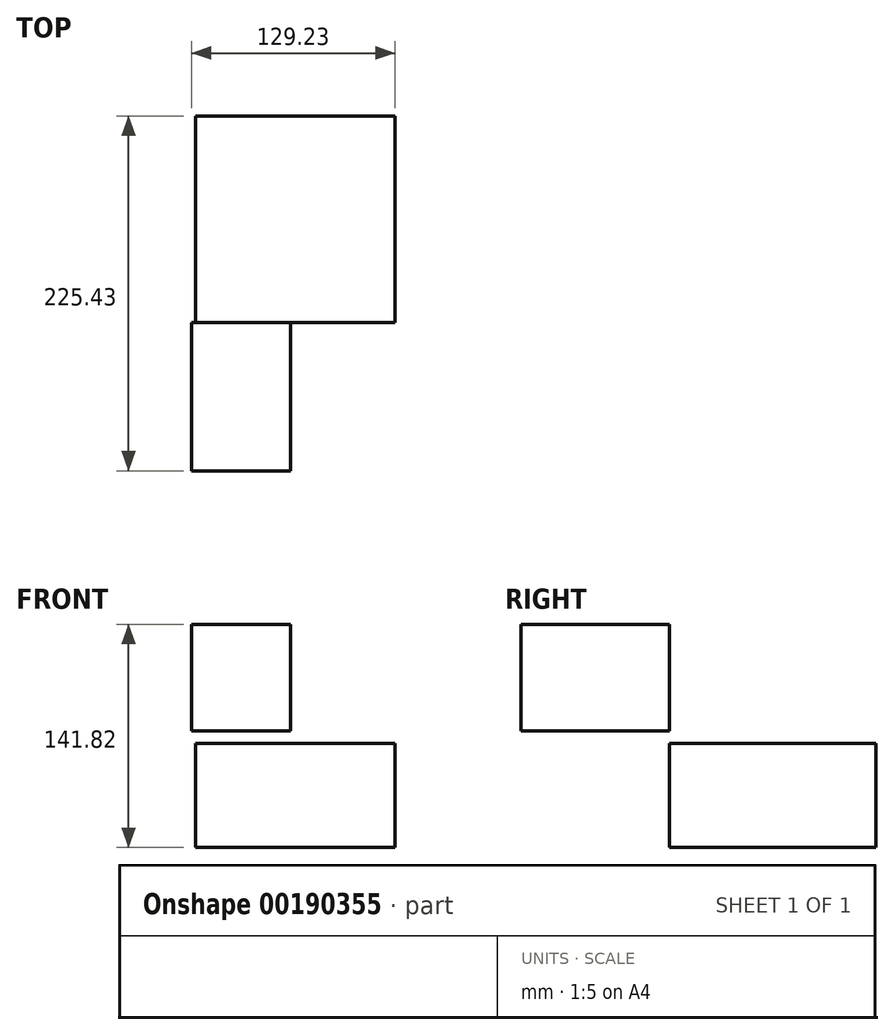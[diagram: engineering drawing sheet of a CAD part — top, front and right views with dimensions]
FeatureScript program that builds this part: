
annotation { "Feature Type Name" : "Feature", "Feature Type Description" : "" }
export const myFeature = defineFeature(function(context is Context, id is Id, definition is map)
    precondition{}
    {
        {
            var Q0;
            Q0=qCreatedBy(makeId("Front.planeOp"),FACE);
            var sketch = newSketch(context, id + "F0", { "sketchPlane" : qUnion([Q0])});
            skLineSegment(sketch, "E0.bottom", {"start": v(-27.24, 41.2) * mm, "end": v(35.73, 41.2) * mm});
            skLineSegment(sketch, "E0.top", {"start": v(-27.24, -26.42) * mm, "end": v(35.73, -26.42) * mm});
            skLineSegment(sketch, "E0.left", {"start": v(-27.24, 41.2) * mm, "end": v(-27.24, -26.42) * mm});
            skLineSegment(sketch, "E0.right", {"start": v(35.73, 41.2) * mm, "end": v(35.73, -26.42) * mm});
            skSolve(sketch);
        }
        {
            var Q0;
            Q0=makeQuery(id+"F0.imprint","IMPRINT",FACE,{"disambiguationData":[TD([[makeQuery(id+"F0.imprint","IMPRINT",EDGE,{"derivedFrom":sQuery(id+"F0.wireOp",EDGE,"E0.bottom")}),-1.0]])]});
            extrude(context, id + "F5", {"entities" : qUnion([Q0]), "depth" : 94.3 * mm});
        }
        {
            var Q0;
            Q0=makeQuery(id+"F5.opExtrude","CAP_FACE",FACE,{"disambiguationData":[OSD([sQuery(id+"F0.wireOp",EDGE,"E0.bottom"),sQuery(id+"F0.wireOp",EDGE,"E0.top"),sQuery(id+"F0.wireOp",EDGE,"E0.left"),sQuery(id+"F0.wireOp",EDGE,"E0.right")])],"isStart":false});
            var sketch = newSketch(context, id + "F1", { "sketchPlane" : qUnion([Q0])});
            skSolve(sketch);
        }
        {
            var Q0;
            Q0=makeQuery(id+"F1.imprint","IMPRINT",FACE,{"disambiguationData":[TD([[makeQuery(id+"F1.imprint","IMPRINT",EDGE,{"derivedFrom":makeQuery(id+"F5.opExtrude","CAP_EDGE",EDGE,{"disambiguationData":[OSD([sQuery(id+"F0.wireOp",EDGE,"E0.bottom")])],"isStart":false})}),-1.0]])]});
            cPlane(context, id + "F2", {"entities" : qUnion([Q0]), "cplaneType" : CPlaneType.OFFSET, "offset" : 25.4 * mm, "width" : 152.4 * mm, "height" : 152.4 * mm});
        }
        {
            var Q0;
            Q0=qCreatedBy(makeId("Front.planeOp"), FACE);
            var sketch = newSketch(context, id + "F3", { "sketchPlane" : qUnion([Q0])});
            skLineSegment(sketch, "E1.bottom", {"start": v(102, -100.63) * mm, "end": v(-24.76, -100.63) * mm});
            skLineSegment(sketch, "E1.top", {"start": v(102, -34.5) * mm, "end": v(-24.76, -34.5) * mm});
            skLineSegment(sketch, "E1.left", {"start": v(102, -100.63) * mm, "end": v(102, -34.5) * mm});
            skLineSegment(sketch, "E1.right", {"start": v(-24.76, -100.63) * mm, "end": v(-24.76, -34.5) * mm});
            skSolve(sketch);
        }
        {
            var Q0;
            Q0 = qSketchRegion(id + "F3", true);
            extrude(context, id + "F4", {"entities" : qUnion([Q0]), "oppositeDirection" : true, "depth" : 131.14 * mm, "offsetDistance" : 25 * mm});
        }
    });
